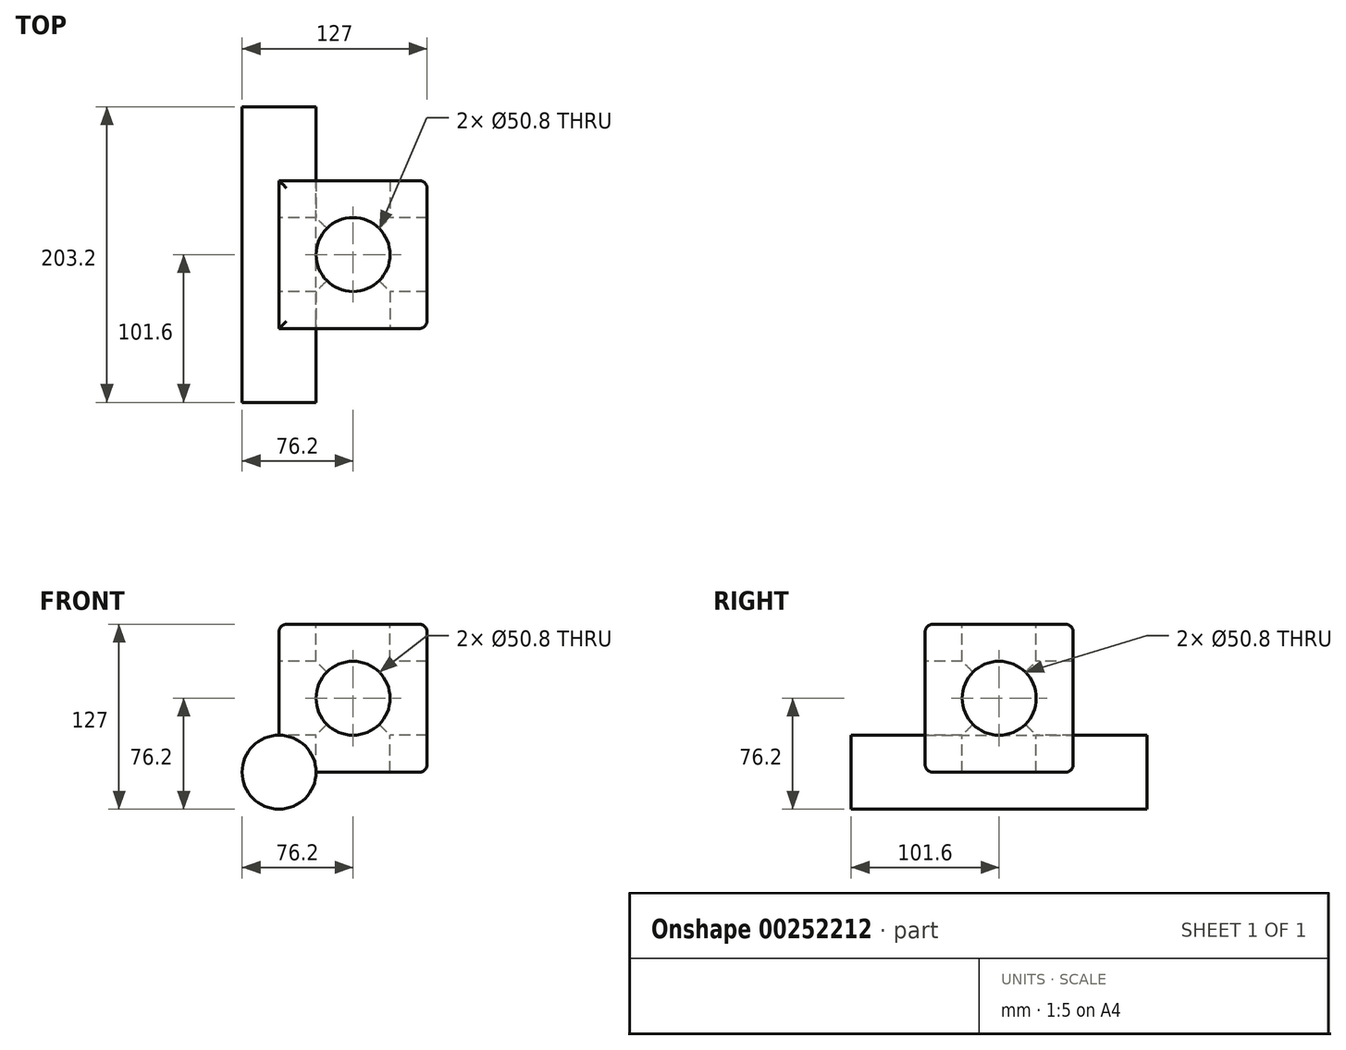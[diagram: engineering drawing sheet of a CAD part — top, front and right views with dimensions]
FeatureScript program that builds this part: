
annotation { "Feature Type Name" : "Feature", "Feature Type Description" : "" }
export const myFeature = defineFeature(function(context is Context, id is Id, definition is map)
    precondition{}
    {
        {
            var Q0;
            Q0=qCreatedBy(makeId("Front.planeOp"),FACE);
            var sketch = newSketch(context, id + "F0", { "sketchPlane" : qUnion([Q0])});
            skLineSegment(sketch, "E0", {"start": v(0, 0) * mm, "end": v(101.6, 0) * mm});
            skLineSegment(sketch, "E1", {"start": v(101.6, 0) * mm, "end": v(101.6, 101.6) * mm});
            skLineSegment(sketch, "E2", {"start": v(101.6, 101.6) * mm, "end": v(0, 101.6) * mm});
            skLineSegment(sketch, "E3", {"start": v(0, 0) * mm, "end": v(0, 101.6) * mm});
            skSolve(sketch);
        }
        {
            var Q0;
            Q0=makeQuery(id+"F0.imprint","IMPRINT",FACE,{"disambiguationData":[TD([[makeQuery(id+"F0.imprint","IMPRINT",EDGE,{"derivedFrom":sQuery(id+"F0.wireOp",EDGE,"E0")}),1.0]])]});
            extrude(context, id + "F1", {"entities" : qUnion([Q0]), "depth" : 101.6 * mm});
        }
        {
            var Q0;
            Q0=makeQuery(id+"F1.opExtrude","SWEPT_FACE",FACE,{"disambiguationData":[OSD([sQuery(id+"F0.wireOp",EDGE,"E2")])]});
            var sketch = newSketch(context, id + "F2", { "sketchPlane" : qUnion([Q0])});
            skCircle(sketch, "E4", {"center": v(50.8, -50.8) * mm, "radius": 25.4 * mm});
            skPoint(sketch, "E5.orphan", {"position": v(50.8, 0) * mm});
            skPoint(sketch, "E6.end.orphan", {"position": v(50.8, -101.6) * mm});
            skSolve(sketch);
        }
        {
            var Q0;
            Q0=makeQuery(id+"F2.imprint","IMPRINT",FACE,{"disambiguationData":[TD([[makeQuery(id+"F2.imprint","IMPRINT",EDGE,{"derivedFrom":sQuery(id+"F2.wireOp",EDGE,"E4")}),1.0]])]});
            extrude(context, id + "F3", {"entities" : qUnion([Q0]), "operationType" : NewBodyOperationType.REMOVE, "oppositeDirection" : true, "depth" : 101.6 * mm});
        }
        {
            var Q0;
            Q0=makeQuery(id+"F1.opExtrude","SWEPT_FACE",FACE,{"disambiguationData":[OSD([sQuery(id+"F0.wireOp",EDGE,"E3")])]});
            var sketch = newSketch(context, id + "F4", { "sketchPlane" : qUnion([Q0])});
            skCircle(sketch, "E7", {"center": v(50.8, 50.8) * mm, "radius": 25.4 * mm});
            skPoint(sketch, "E8.orphan", {"position": v(50.8, 101.6) * mm});
            skPoint(sketch, "E9.end.orphan", {"position": v(50.8, 0) * mm});
            skSolve(sketch);
        }
        {
            var Q0;
            Q0 = qSketchRegion(id + "F4", true);
            extrude(context, id + "F5", {"entities" : qUnion([Q0]), "operationType" : NewBodyOperationType.REMOVE, "oppositeDirection" : true, "depth" : 101.6 * mm});
        }
        {
            var Q0;
            Q0=makeQuery(id+"F1.opExtrude","CAP_FACE",FACE,{"disambiguationData":[OSD([sQuery(id+"F0.wireOp",EDGE,"E0"),sQuery(id+"F0.wireOp",EDGE,"E1"),sQuery(id+"F0.wireOp",EDGE,"E2"),sQuery(id+"F0.wireOp",EDGE,"E3")])],"isStart":false});
            var sketch = newSketch(context, id + "F6", { "sketchPlane" : qUnion([Q0])});
            skLineSegment(sketch, "E10", {"start": v(50.8, 101.6) * mm, "end": v(50.8, 0) * mm});
            skCircle(sketch, "E11", {"center": v(50.8, 50.8) * mm, "radius": 25.4 * mm});
            skSolve(sketch);
        }
        {
            var Q0;
            Q0 = qSketchRegion(id + "F6", true);
            extrude(context, id + "F7", {"entities" : qUnion([Q0]), "operationType" : NewBodyOperationType.REMOVE, "oppositeDirection" : true, "depth" : 101.6 * mm});
        }
        {
            var Q0;
            Q0=makeQuery(id+"F1.opExtrude","CAP_EDGE",EDGE,{"disambiguationData":[OSD([sQuery(id+"F0.wireOp",EDGE,"E2")])],"isStart":false});
            var Q1;
            Q1=makeQuery(id+"F1.opExtrude","SWEPT_EDGE",EDGE,{"disambiguationData":[OSD([sQuery(id+"F0.wireOp",EDGE,"E1"),sQuery(id+"F0.wireOp",EDGE,"E2")])]});
            var Q2;
            Q2=makeQuery(id+"F1.opExtrude","CAP_EDGE",EDGE,{"disambiguationData":[OSD([sQuery(id+"F0.wireOp",EDGE,"E2")])],"isStart":true});
            var Q3;
            Q3=makeQuery(id+"F1.opExtrude","SWEPT_EDGE",EDGE,{"disambiguationData":[OSD([sQuery(id+"F0.wireOp",EDGE,"E2"),sQuery(id+"F0.wireOp",EDGE,"E3")])]});
            var Q4;
            Q4=makeQuery(id+"F1.opExtrude","SWEPT_EDGE",EDGE,{"disambiguationData":[OSD([sQuery(id+"F0.wireOp",EDGE,"E0"),sQuery(id+"F0.wireOp",EDGE,"E1")])]});
            var Q5;
            Q5=makeQuery(id+"F1.opExtrude","CAP_EDGE",EDGE,{"disambiguationData":[OSD([sQuery(id+"F0.wireOp",EDGE,"E0")])],"isStart":false});
            var Q6;
            Q6=makeQuery(id+"F1.opExtrude","SWEPT_EDGE",EDGE,{"disambiguationData":[OSD([sQuery(id+"F0.wireOp",EDGE,"E0"),sQuery(id+"F0.wireOp",EDGE,"E3")])]});
            var Q7;
            Q7=makeQuery(id+"F1.opExtrude","CAP_EDGE",EDGE,{"disambiguationData":[OSD([sQuery(id+"F0.wireOp",EDGE,"E0")])],"isStart":true});
            var Q8;
            Q8=makeQuery(id+"F1.opExtrude","CAP_EDGE",EDGE,{"disambiguationData":[OSD([sQuery(id+"F0.wireOp",EDGE,"E1")])],"isStart":true});
            fillet(context, id + "F8", {"entities" : qUnion([Q0, Q1, Q2, Q3, Q4, Q5, Q6, Q7, Q8]), "radius" : 5.08 * mm, "tangentPropagation" : true, "allowEdgeOverflow" : false});
        }
        {
            var Q0;
            Q0=qCreatedBy(makeId("Front.planeOp"),FACE);
            cPlane(context, id + "F9", {"entities" : qUnion([Q0]), "cplaneType" : CPlaneType.OFFSET, "offset" : 101.6 * mm, "width" : 152.4 * mm, "height" : 152.4 * mm});
        }
        {
            var Q0;
            Q0=makeQuery(id+"F1.opExtrude","CAP_EDGE",EDGE,{"disambiguationData":[OSD([sQuery(id+"F0.wireOp",EDGE,"E1")])],"isStart":false});
            fillet(context, id + "F10", {"entities" : qUnion([Q0]), "radius" : 5.08 * mm, "tangentPropagation" : true, "allowEdgeOverflow" : false});
        }
        {
            var Q0;
            Q0=qCreatedBy(id+"F9.planeOp",FACE);
            var sketch = newSketch(context, id + "F11", { "sketchPlane" : qUnion([Q0])});
            skCircle(sketch, "E12", {"center": v(0, 0) * mm, "radius": 25.4 * mm});
            skSolve(sketch);
        }
        {
            var Q0;
            Q0 = qSketchRegion(id + "F11", true);
            extrude(context, id + "F12", {"entities" : qUnion([Q0]), "operationType" : NewBodyOperationType.ADD, "depth" : 50.8 * mm, "hasSecondDirection" : true, "secondDirectionOppositeDirection" : true, "secondDirectionDepth" : 152.4 * mm});
        }
    });
